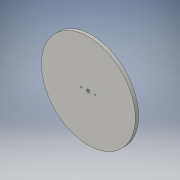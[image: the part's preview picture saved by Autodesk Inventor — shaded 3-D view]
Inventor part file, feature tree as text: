
AUTODESK INVENTOR PART (.ipt)
format: ipt  version: 2016 (Build 200138000, 138)  size: 103,424 bytes
history: native  units: in
note: dims shown in document units (in); Inventor stores cm internally (conversion verified against a paired STEP export)
features: sketch x2, extrude x1
ambient origin geometry x8: Origin, YZ Plane, XZ Plane, XY Plane, X Axis, Y Axis, Z Axis, Center Point
bodies: Solid1 (feature_tree)
feature tree (3):
  extrude  "Extrusion1"  Depth=0.375in
  sketch  "Sketch3"  dims[d3=0.375in d4=0.075in d5=0.075in d6=0.175in d7=0.18in d8=0.0in]
  sketch  "Sketch1"  dims[d0=5.0in d2=0.375in]
